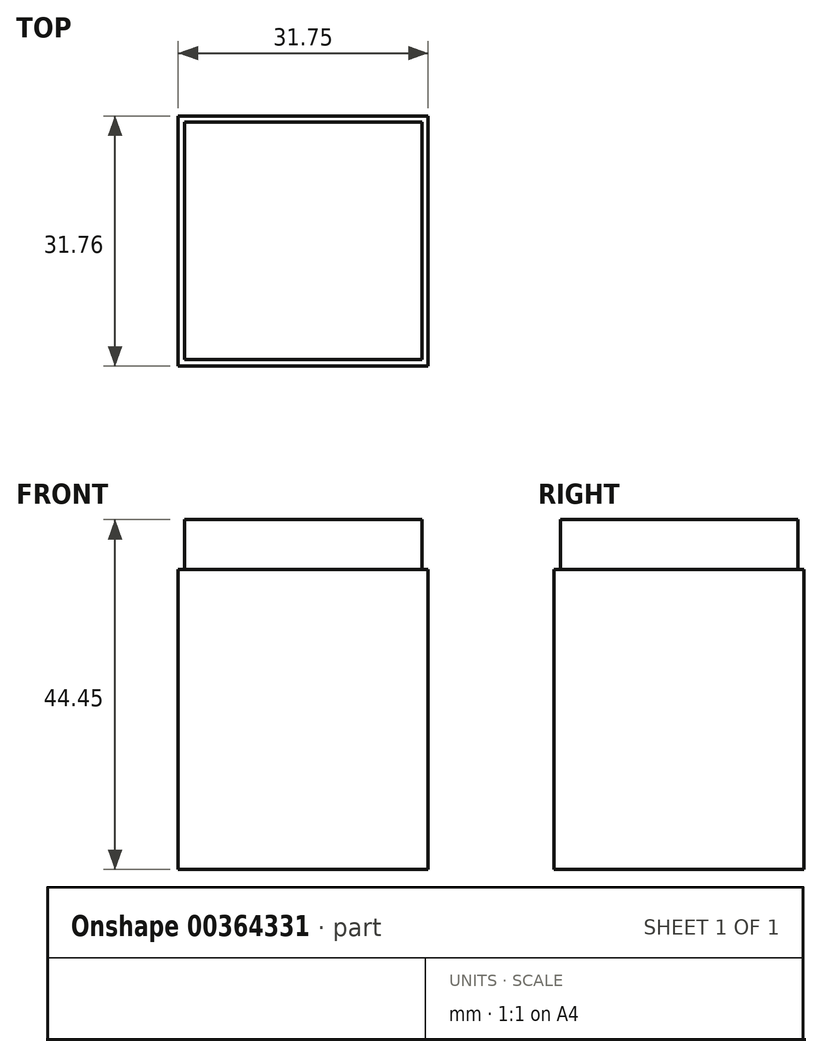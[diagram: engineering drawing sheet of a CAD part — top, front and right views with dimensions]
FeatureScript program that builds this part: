
annotation { "Feature Type Name" : "Feature", "Feature Type Description" : "" }
export const myFeature = defineFeature(function(context is Context, id is Id, definition is map)
    precondition{}
    {
        {
            var Q0;
            Q0=qCreatedBy(makeId("Right.planeOp"),FACE);
            var sketch = newSketch(context, id + "F0", { "sketchPlane" : qUnion([Q0])});
            skLineSegment(sketch, "E0", {"start": v(0, 0) * mm, "end": v(-15.88, 0) * mm});
            skLineSegment(sketch, "E1", {"start": v(-15.88, 0) * mm, "end": v(-15.88, 38.1) * mm});
            skLineSegment(sketch, "E2", {"start": v(-15.88, 38.1) * mm, "end": v(-15.08, 38.1) * mm});
            skLineSegment(sketch, "E3", {"start": v(-15.08, 38.1) * mm, "end": v(-15.08, 44.45) * mm});
            skLineSegment(sketch, "E4", {"start": v(-15.08, 44.45) * mm, "end": v(0, 44.45) * mm});
            skLineSegment(sketch, "E5", {"start": v(0, 38.78) * mm, "end": v(0, -3.4) * mm, "construction": true});
            skLineSegment(sketch, "E6.MirrorCS", {"start": v(15.08, 44.45) * mm, "end": v(0, 44.45) * mm});
            skLineSegment(sketch, "E7.MirrorCS", {"start": v(15.88, 0) * mm, "end": v(15.88, 38.1) * mm});
            skLineSegment(sketch, "E8.MirrorCS", {"start": v(0, 0) * mm, "end": v(15.88, 0) * mm});
            skLineSegment(sketch, "E9.MirrorCS", {"start": v(15.88, 38.1) * mm, "end": v(15.08, 38.1) * mm});
            skLineSegment(sketch, "E10.MirrorCS", {"start": v(15.08, 38.1) * mm, "end": v(15.08, 44.45) * mm});
            skSolve(sketch);
        }
        {
            var Q0;
            Q0=makeQuery(id+"F0.imprint","IMPRINT",FACE,{"disambiguationData":[TD([[makeQuery(id+"F0.imprint","IMPRINT",EDGE,{"derivedFrom":sQuery(id+"F0.wireOp",EDGE,"E0")}),-1.0]])]});
            extrude(context, id + "F1", {"entities" : qUnion([Q0]), "depth" : 31.75 * mm});
        }
        {
            var Q0;
            Q0=makeQuery(id+"F1.opExtrude","SWEPT_FACE",FACE,{"disambiguationData":[OSD([sQuery(id+"F0.wireOp",EDGE,"E3")])]});
            var sketch = newSketch(context, id + "F2", { "sketchPlane" : qUnion([Q0])});
            skLineSegment(sketch, "E11", {"start": v(30.96, 44.45) * mm, "end": v(30.96, 38.1) * mm});
            skLineSegment(sketch, "E12", {"start": v(0.8, 44.45) * mm, "end": v(0.8, 38.1) * mm});
            skSolve(sketch);
        }
        {
            var Q0;
            Q0 = qSketchRegion(id + "F2", true);
            var Q1;
            {var subQ0=sQuery(id+"F2.wireOp",EDGE,"E12");Q1=makeQuery(id+"F2.imprint","IMPRINT",FACE,{"disambiguationData":[TD([[makeQuery(id+"F2.imprint","IMPRINT",EDGE,{"derivedFrom":subQ0}),-1.0]])]});}
            var Q2;
            {var subQ0=sQuery(id+"F2.wireOp",EDGE,"E11");Q2=makeQuery(id+"F2.imprint","IMPRINT",FACE,{"disambiguationData":[TD([[makeQuery(id+"F2.imprint","IMPRINT",EDGE,{"derivedFrom":subQ0}),1.0]])]});}
            extrude(context, id + "F3", {"entities" : qUnion([Q0, Q1, Q2]), "operationType" : NewBodyOperationType.REMOVE, "endBound" : BoundingType.UP_TO_NEXT, "oppositeDirection" : true, "depth" : 25.4 * mm});
        }
    });
